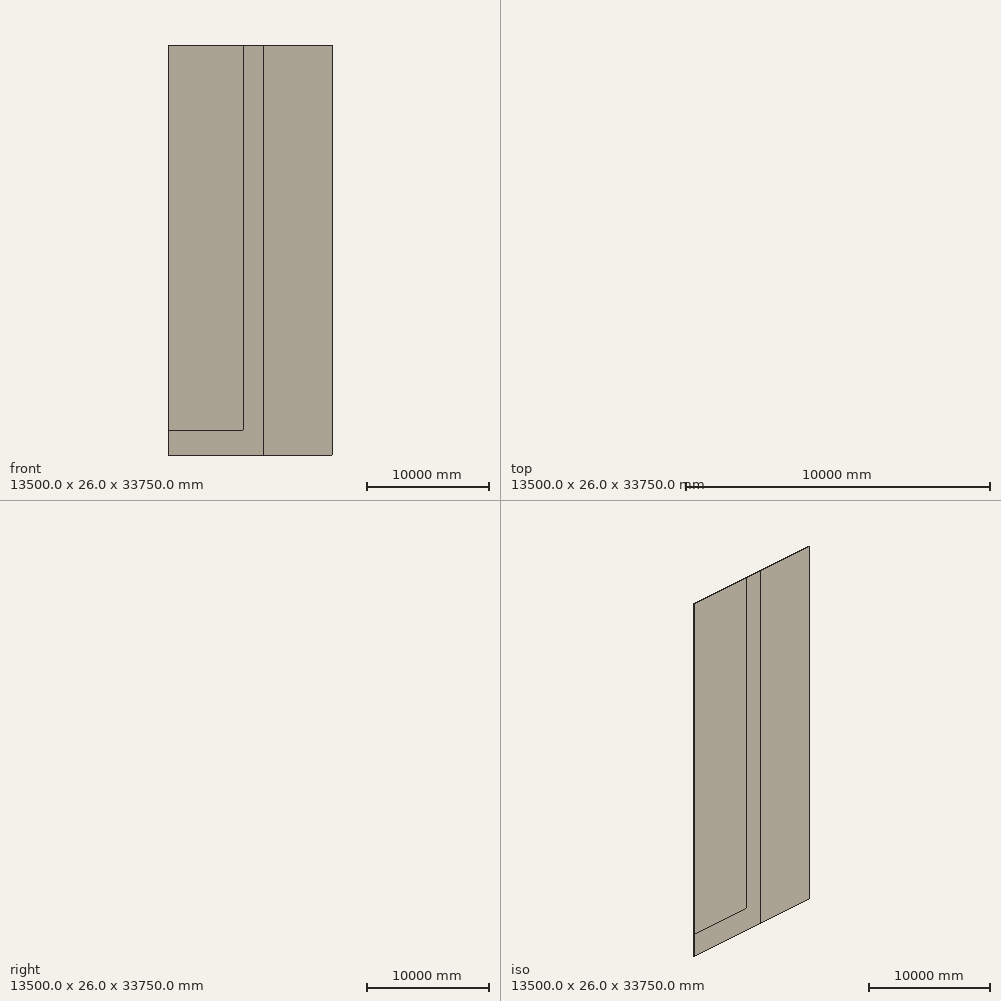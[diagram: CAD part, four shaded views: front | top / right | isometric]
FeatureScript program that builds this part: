
annotation { "Feature Type Name" : "Feature", "Feature Type Description" : "" }
export const myFeature = defineFeature(function(context is Context, id is Id, definition is map)
    precondition{}
    {
        {
            var Q0;
            Q0=qCreatedBy(makeId("Front.planeOp"),FACE);
            var sketch = newSketch(context, id + "F0", { "sketchPlane" : qUnion([Q0])});
            skLineSegment(sketch, "E0.0.1.0", {"start": v(6750, 3750) * mm, "end": v(-6750, 3750) * mm, "construction": true});
            skLineSegment(sketch, "E0.0.2.0", {"start": v(6750, 7500) * mm, "end": v(-6750, 7500) * mm, "construction": true});
            skLineSegment(sketch, "E0.0.3.0", {"start": v(6750, 11250) * mm, "end": v(-6750, 11250) * mm, "construction": true});
            skLineSegment(sketch, "E0.0.4.0", {"start": v(6750, 15000) * mm, "end": v(-6750, 15000) * mm, "construction": true});
            skLineSegment(sketch, "E0.0.5.0", {"start": v(6750, 18750) * mm, "end": v(-6750, 18750) * mm, "construction": true});
            skLineSegment(sketch, "E0.0.6.0", {"start": v(6750, 22500) * mm, "end": v(-6750, 22500) * mm, "construction": true});
            skLineSegment(sketch, "E0.0.7.0", {"start": v(6750, 26250) * mm, "end": v(-6750, 26250) * mm, "construction": true});
            skLineSegment(sketch, "E0.0.8.0", {"start": v(6750, 30000) * mm, "end": v(-6750, 30000) * mm, "construction": true});
            skLineSegment(sketch, "E0.0.9.0", {"start": v(6750, 33750) * mm, "end": v(-6750, 33750) * mm, "construction": true});
            skLineSegment(sketch, "E1.bottom", {"start": v(-6750, 33750) * mm, "end": v(-150, 33750) * mm});
            skLineSegment(sketch, "E2.top", {"start": v(6750, 33750) * mm, "end": v(1050, 33750) * mm});
            skLineSegment(sketch, "E3.0.1.0", {"start": v(6750, 0) * mm, "end": v(-6750, 0) * mm, "construction": true});
            skLineSegment(sketch, "E3.direction1", {"start": v(-6750, 3750) * mm, "end": v(-6725, 3750) * mm, "construction": true});
            skLineSegment(sketch, "E4", {"start": v(-6750, 33750) * mm, "end": v(-6750, 0) * mm});
            skLineSegment(sketch, "E5", {"start": v(6750, 33750) * mm, "end": v(6750, 0) * mm});
            skLineSegment(sketch, "E6", {"start": v(-6750, 0) * mm, "end": v(6750, 0) * mm});
            skLineSegment(sketch, "E7", {"start": v(-6750, 33750) * mm, "end": v(6750, 33750) * mm});
            skSolve(sketch);
        }
        {
            var Q0;
            Q0 = qSketchRegion(id + "F0", true);
            extrude(context, id + "F1", {"entities" : qUnion([Q0]), "depth" : 25 * mm});
        }
        {
            var Q0;
            Q0=makeQuery(id+"F1.opExtrude","CAP_FACE",FACE,{"disambiguationData":[OSD([sQuery(id+"F0.wireOp",EDGE,"E4"),sQuery(id+"F0.wireOp",EDGE,"E5"),sQuery(id+"F0.wireOp",EDGE,"E6"),sQuery(id+"F0.wireOp",EDGE,"E7")])],"isStart":false});
            var sketch = newSketch(context, id + "F2", { "sketchPlane" : qUnion([Q0])});
            skLineSegment(sketch, "E8", {"start": v(-6750, 0) * mm, "end": v(6750, 0) * mm, "construction": true});
            skLineSegment(sketch, "E9.0.1.0", {"start": v(-6750, 3750) * mm, "end": v(6750, 3750) * mm, "construction": true});
            skLineSegment(sketch, "E9.0.2.0", {"start": v(-6750, 7500) * mm, "end": v(6750, 7500) * mm, "construction": true});
            skLineSegment(sketch, "E9.0.3.0", {"start": v(-6750, 11250) * mm, "end": v(6750, 11250) * mm, "construction": true});
            skLineSegment(sketch, "E9.0.4.0", {"start": v(-6750, 15000) * mm, "end": v(6750, 15000) * mm, "construction": true});
            skLineSegment(sketch, "E9.0.5.0", {"start": v(-6750, 18750) * mm, "end": v(6750, 18750) * mm, "construction": true});
            skLineSegment(sketch, "E9.0.6.0", {"start": v(-6750, 22500) * mm, "end": v(6750, 22500) * mm, "construction": true});
            skLineSegment(sketch, "E9.0.7.0", {"start": v(-6750, 26250) * mm, "end": v(6750, 26250) * mm, "construction": true});
            skLineSegment(sketch, "E9.direction1", {"start": v(-6750, 0) * mm, "end": v(-6725, 0) * mm, "construction": true});
            skLineSegment(sketch, "E9.direction2", {"start": v(-6750, 0) * mm, "end": v(-6750, 3750) * mm, "construction": true});
            skLineSegment(sketch, "E10.0.0.8", {"start": v(-6750, 30000) * mm, "end": v(6750, 30000) * mm, "construction": true});
            skLineSegment(sketch, "E10.0.0.9", {"start": v(-6750, 33750) * mm, "end": v(6750, 33750) * mm, "construction": true});
            skLineSegment(sketch, "E11.bottom", {"start": v(-6750, 33750) * mm, "end": v(-550, 33750) * mm});
            skLineSegment(sketch, "E11.top", {"start": v(-6750, 2100) * mm, "end": v(-550, 2100) * mm});
            skLineSegment(sketch, "E11.left", {"start": v(-6750, 33750) * mm, "end": v(-6750, 2100) * mm});
            skLineSegment(sketch, "E11.right", {"start": v(-550, 33750) * mm, "end": v(-550, 2100) * mm});
            skLineSegment(sketch, "E12.bottom", {"start": v(6750, 0) * mm, "end": v(1050, 0) * mm});
            skLineSegment(sketch, "E12.top", {"start": v(6750, 33750) * mm, "end": v(1050, 33750) * mm});
            skLineSegment(sketch, "E12.left", {"start": v(6750, 0) * mm, "end": v(6750, 33750) * mm});
            skLineSegment(sketch, "E12.right", {"start": v(1050, 0) * mm, "end": v(1050, 33750) * mm});
            skSolve(sketch);
        }
        {
            var Q0;
            Q0 = qSketchRegion(id + "F2", true);
            extrude(context, id + "F3", {"entities" : qUnion([Q0]), "operationType" : NewBodyOperationType.ADD, "depth" : 1 * mm});
        }
    });
